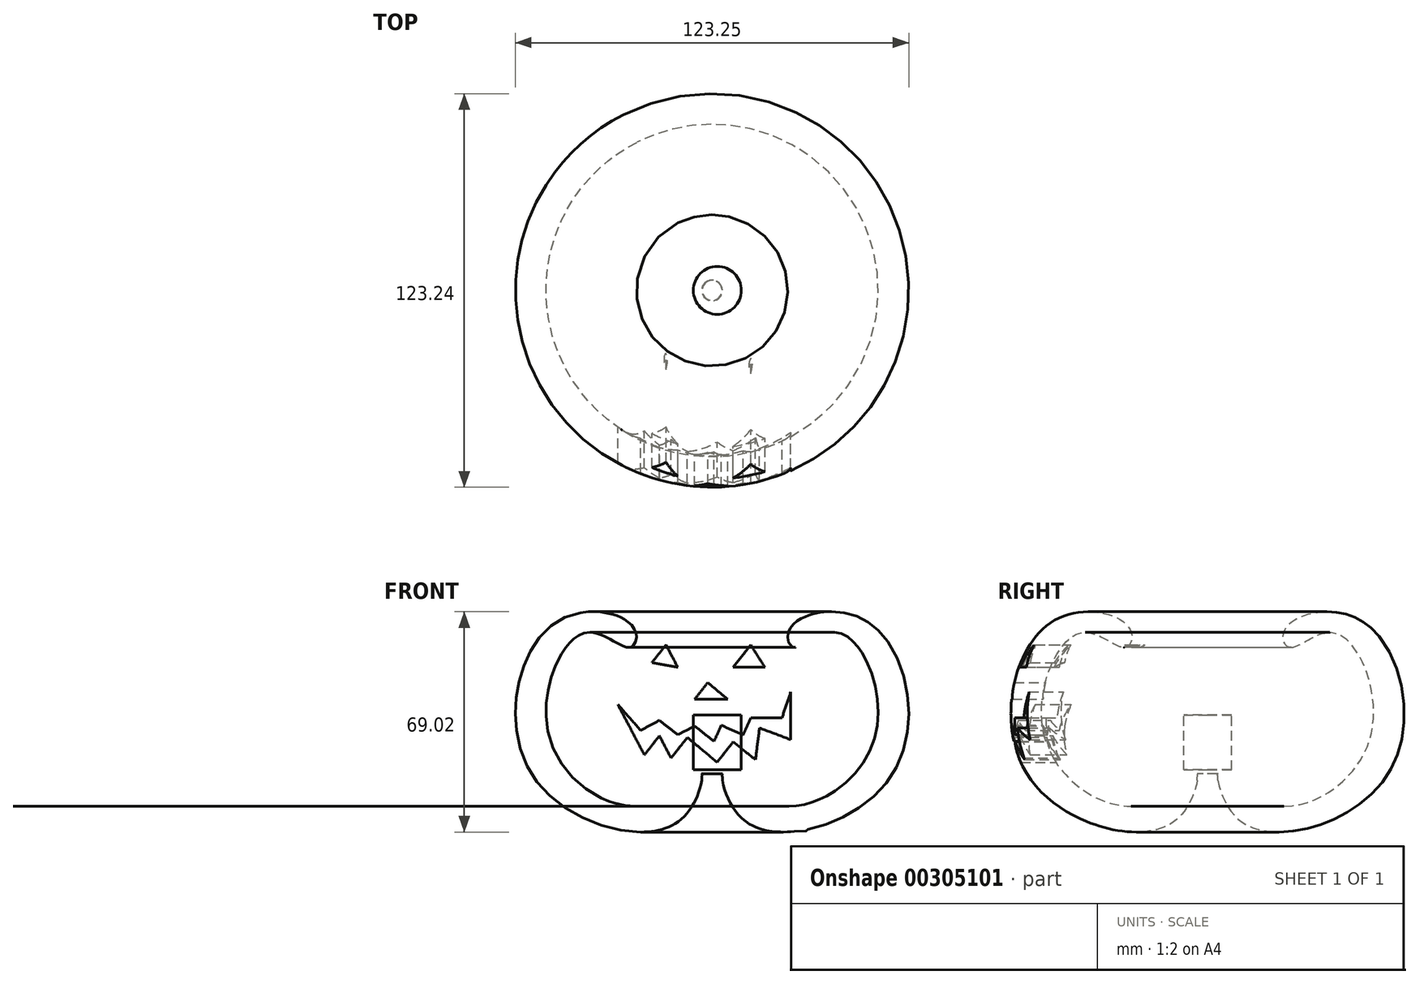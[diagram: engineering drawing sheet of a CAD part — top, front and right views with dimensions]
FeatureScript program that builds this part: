
annotation { "Feature Type Name" : "Feature", "Feature Type Description" : "" }
export const myFeature = defineFeature(function(context is Context, id is Id, definition is map)
    precondition{}
    {
        {
            var Q0;
            Q0=qCreatedBy(makeId("Front.planeOp"),FACE);
            var sketch = newSketch(context, id + "F0", { "sketchPlane" : qUnion([Q0])});
            skFitSpline(sketch, "E0", {"points": [v(21.23, 16.3) * mm, v(45.46, 18.37) * mm, v(53.37, -29.31) * mm, v(8.54, -45.05) * mm, v(0, -31.52) * mm, v(0, -31.13) * mm, v(0, -30.3) * mm, v(0, -29.3) * mm, v(16.76, -39.05) * mm, v(47.95, -17.32) * mm, v(36.1, 14.92) * mm, v(22.5, 10.32) * mm, v(21.23, 16.3) * mm]});
            skLineSegment(sketch, "E1", {"start": v(-3.23, 49.04) * mm, "end": v(-3.23, 11.8) * mm});
            skLineSegment(sketch, "E2", {"start": v(-15.96, 11.06) * mm, "end": v(-20.38, 5.53) * mm});
            skLineSegment(sketch, "E3", {"start": v(-20.38, 5.53) * mm, "end": v(-12.27, 4.06) * mm});
            skLineSegment(sketch, "E4", {"start": v(-12.27, 4.06) * mm, "end": v(-15.96, 11.06) * mm});
            skLineSegment(sketch, "E5", {"start": v(10.59, 11.06) * mm, "end": v(5.06, 4.06) * mm});
            skLineSegment(sketch, "E6", {"start": v(5.06, 4.06) * mm, "end": v(15.01, 4.06) * mm});
            skLineSegment(sketch, "E7", {"start": v(15.01, 4.06) * mm, "end": v(10.59, 11.06) * mm});
            skLineSegment(sketch, "E8", {"start": v(-2.87, -0.74) * mm, "end": v(-7.01, -5.99) * mm});
            skLineSegment(sketch, "E9", {"start": v(-7.01, -5.99) * mm, "end": v(3.4, -5.99) * mm});
            skLineSegment(sketch, "E10", {"start": v(3.4, -5.99) * mm, "end": v(-2.87, -0.74) * mm});
            skLineSegment(sketch, "E11", {"start": v(-27.57, -14.2) * mm, "end": v(-22.74, -23.38) * mm});
            skLineSegment(sketch, "E12", {"start": v(-22.74, -23.38) * mm, "end": v(-18.03, -17.41) * mm});
            skLineSegment(sketch, "E13", {"start": v(-18.03, -17.41) * mm, "end": v(-14.37, -24.37) * mm});
            skLineSegment(sketch, "E14", {"start": v(-14.37, -24.37) * mm, "end": v(-9.26, -17.9) * mm});
            skLineSegment(sketch, "E15", {"start": v(-9.26, -17.9) * mm, "end": v(0.04, -25.69) * mm});
            skLineSegment(sketch, "E16", {"start": v(0.04, -25.69) * mm, "end": v(5.06, -19.32) * mm});
            skLineSegment(sketch, "E17", {"start": v(5.06, -19.32) * mm, "end": v(12.06, -24.85) * mm});
            skLineSegment(sketch, "E18", {"start": v(12.06, -24.85) * mm, "end": v(13.35, -14.93) * mm});
            skLineSegment(sketch, "E19", {"start": v(13.35, -14.93) * mm, "end": v(23.12, -18.62) * mm});
            skLineSegment(sketch, "E20", {"start": v(23.12, -18.62) * mm, "end": v(23.12, -3.69) * mm});
            skLineSegment(sketch, "E21", {"start": v(23.12, -3.69) * mm, "end": v(20.36, -11.8) * mm});
            skLineSegment(sketch, "E22", {"start": v(20.36, -11.8) * mm, "end": v(10.59, -11.8) * mm});
            skLineSegment(sketch, "E23", {"start": v(10.59, -11.8) * mm, "end": v(8.2, -17.15) * mm});
            skLineSegment(sketch, "E24", {"start": v(8.2, -17.15) * mm, "end": v(1.36, -14.08) * mm});
            skLineSegment(sketch, "E25", {"start": v(1.36, -14.08) * mm, "end": v(-0.91, -19.14) * mm});
            skLineSegment(sketch, "E26", {"start": v(-0.91, -19.14) * mm, "end": v(-7.01, -14.33) * mm});
            skLineSegment(sketch, "E27", {"start": v(-7.01, -14.33) * mm, "end": v(-12.27, -17.1) * mm});
            skLineSegment(sketch, "E28", {"start": v(-12.27, -17.1) * mm, "end": v(-18, -12.57) * mm});
            skLineSegment(sketch, "E29", {"start": v(-18, -12.57) * mm, "end": v(-23.9, -15.67) * mm});
            skLineSegment(sketch, "E30", {"start": v(-23.9, -15.67) * mm, "end": v(-31.08, -7.56) * mm});
            skLineSegment(sketch, "E31", {"start": v(-31.08, -7.56) * mm, "end": v(-27.57, -14.2) * mm});
            skSolve(sketch);
        }
        {
            var Q0;
            Q0=makeQuery(id+"F0.imprint","IMPRINT",FACE,{"disambiguationData":[TD([[makeQuery(id+"F0.imprint","IMPRINT",EDGE,{"derivedFrom":sQuery(id+"F0.wireOp",EDGE,"E0")}),-1.0]])]});
            var Q1;
            Q1=sQuery(id+"F0.wireOp",EDGE,"E1");
            revolve(context, id + "F1", {"entities" : qUnion([Q0]), "axis" : qUnion([Q1]), "revolveType" : RevolveType.FULL});
        }
        {
            var Q0;
            Q0=qCreatedBy(makeId("Front.planeOp"),FACE);
            var sketch = newSketch(context, id + "F2", { "sketchPlane" : qUnion([Q0])});
            skLineSegment(sketch, "E32", {"start": v(-17.66, 11.07) * mm, "end": v(-22.08, 5.54) * mm});
            skLineSegment(sketch, "E33", {"start": v(-22.08, 5.54) * mm, "end": v(-13.97, 4.07) * mm});
            skLineSegment(sketch, "E34", {"start": v(-13.97, 4.07) * mm, "end": v(-17.66, 11.07) * mm});
            skLineSegment(sketch, "E35", {"start": v(8.89, 11.07) * mm, "end": v(3.36, 4.07) * mm});
            skLineSegment(sketch, "E36", {"start": v(3.36, 4.07) * mm, "end": v(13.31, 4.07) * mm});
            skLineSegment(sketch, "E37", {"start": v(13.31, 4.07) * mm, "end": v(8.89, 11.07) * mm});
            skLineSegment(sketch, "E38", {"start": v(-4.57, -0.72) * mm, "end": v(-8.71, -5.97) * mm});
            skLineSegment(sketch, "E39", {"start": v(-8.71, -5.97) * mm, "end": v(1.7, -5.97) * mm});
            skLineSegment(sketch, "E40", {"start": v(1.7, -5.97) * mm, "end": v(-4.57, -0.72) * mm});
            skLineSegment(sketch, "E41", {"start": v(-29.27, -14.18) * mm, "end": v(-24.44, -23.37) * mm});
            skLineSegment(sketch, "E42", {"start": v(-24.44, -23.37) * mm, "end": v(-19.73, -17.4) * mm});
            skLineSegment(sketch, "E43", {"start": v(-19.73, -17.4) * mm, "end": v(-16.07, -24.36) * mm});
            skLineSegment(sketch, "E44", {"start": v(-16.07, -24.36) * mm, "end": v(-10.96, -17.89) * mm});
            skLineSegment(sketch, "E45", {"start": v(-10.96, -17.89) * mm, "end": v(-1.67, -25.67) * mm});
            skLineSegment(sketch, "E46", {"start": v(-1.67, -25.67) * mm, "end": v(3.36, -19.3) * mm});
            skLineSegment(sketch, "E47", {"start": v(3.36, -19.3) * mm, "end": v(10.36, -24.84) * mm});
            skLineSegment(sketch, "E48", {"start": v(10.36, -24.84) * mm, "end": v(11.65, -14.92) * mm});
            skLineSegment(sketch, "E49", {"start": v(11.65, -14.92) * mm, "end": v(21.42, -18.6) * mm});
            skLineSegment(sketch, "E50", {"start": v(21.42, -18.6) * mm, "end": v(21.42, -3.67) * mm});
            skLineSegment(sketch, "E51", {"start": v(21.42, -3.67) * mm, "end": v(18.66, -11.79) * mm});
            skLineSegment(sketch, "E52", {"start": v(18.66, -11.79) * mm, "end": v(8.89, -11.79) * mm});
            skLineSegment(sketch, "E53", {"start": v(8.89, -11.79) * mm, "end": v(6.5, -17.13) * mm});
            skLineSegment(sketch, "E54", {"start": v(6.5, -17.13) * mm, "end": v(-0.34, -14.07) * mm});
            skLineSegment(sketch, "E55", {"start": v(-0.34, -14.07) * mm, "end": v(-2.61, -19.13) * mm});
            skLineSegment(sketch, "E56", {"start": v(-2.61, -19.13) * mm, "end": v(-8.71, -14.31) * mm});
            skLineSegment(sketch, "E57", {"start": v(-8.71, -14.31) * mm, "end": v(-13.97, -17.08) * mm});
            skLineSegment(sketch, "E58", {"start": v(-13.97, -17.08) * mm, "end": v(-19.7, -12.55) * mm});
            skLineSegment(sketch, "E59", {"start": v(-19.7, -12.55) * mm, "end": v(-25.6, -15.66) * mm});
            skLineSegment(sketch, "E60", {"start": v(-25.6, -15.66) * mm, "end": v(-32.78, -7.55) * mm});
            skLineSegment(sketch, "E61", {"start": v(-32.78, -7.55) * mm, "end": v(-29.27, -14.18) * mm});
            skSolve(sketch);
        }
        {
            var Q0;
            Q0 = qSketchRegion(id + "F2", true);
            extrude(context, id + "F3", {"entities" : qUnion([Q0]), "operationType" : NewBodyOperationType.REMOVE, "depth" : 98.04 * mm});
        }
        {
            var Q0;
            Q0=qCreatedBy(makeId("Front.planeOp"),FACE);
            var sketch = newSketch(context, id + "F4", { "sketchPlane" : qUnion([Q0])});
            skLineSegment(sketch, "E62.bottom", {"start": v(-1.59, -10.86) * mm, "end": v(5.91, -10.86) * mm});
            skLineSegment(sketch, "E62.top", {"start": v(-1.59, -28.05) * mm, "end": v(5.91, -28.05) * mm});
            skLineSegment(sketch, "E62.left", {"start": v(-1.59, -10.86) * mm, "end": v(-1.59, -28.05) * mm});
            skLineSegment(sketch, "E62.right", {"start": v(5.91, -10.86) * mm, "end": v(5.91, -28.05) * mm});
            skSolve(sketch);
        }
        {
            var Q0;
            Q0=makeQuery(id+"F4.imprint","IMPRINT",FACE,{"disambiguationData":[TD([[makeQuery(id+"F4.imprint","IMPRINT",EDGE,{"derivedFrom":sQuery(id+"F4.wireOp",EDGE,"E62.bottom")}),-1.0]])]});
            var Q1;
            Q1=sQuery(id+"F4.wireOp",EDGE,"E62.left");
            revolve(context, id + "F5", {"entities" : qUnion([Q0]), "axis" : qUnion([Q1]), "revolveType" : RevolveType.FULL});
        }
    });
